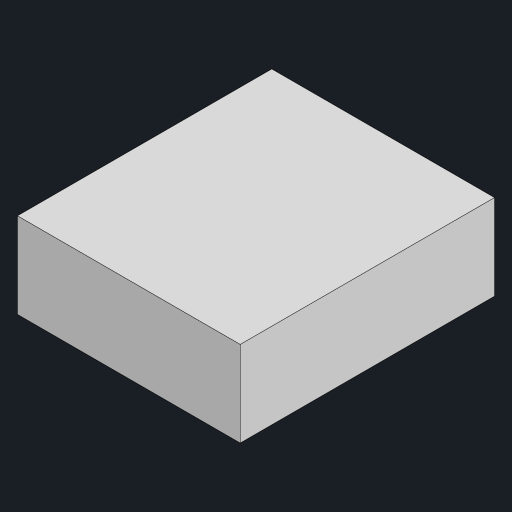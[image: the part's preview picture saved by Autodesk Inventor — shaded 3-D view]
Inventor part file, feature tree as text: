
AUTODESK INVENTOR PART (.ipt)
format: ipt  version: 2023 (Build 270158000, 158)  size: 85,504 bytes
history: native  units: mm
features: other x1, extrude x1, sketch x1
ambient origin geometry x8: Origin, YZ Plane, XZ Plane, XY Plane, X Axis, Y Axis, Z Axis, Center Point
bodies: Body1 (feature_tree)
feature tree (3):
  other  "ソリッド1"
  extrude  "押し出し1"  Depth=12.0mm
  sketch  "スケッチ1"
